# Revit family: LAMP_STORMBELL + OPAL REFLECTOR
name_source: partatom
category: Luminarias
revit_build: Autodesk Revit 2015 (Build: 20140606_1530(x64)
units: mm (PartAtom-declared; Revit-internal decimal feet)

## types (8) — shared parameters
CRI = 80
Diameter = 173 mm  [stored 0.567585 ft]
Fabricante = LAMP
Finish = Shiny white
Gear = Electronic
Height = 173 mm  [stored 0.567585 ft]
IEE = A+
Installation instructions = http://www.lamp.es
Insulation class = I
LED Lifetime = 50.000 L80 B10
Lamp = COB LED
Last update = 11/11/2020
Luminaire type = Indoor - Suspended Downlight
MacAdam = <3
Manufacturer URL = http://www.lamp.es
Manufacturer country = Spain
Manufacturer name = LAMP
Material COB = LAMP_COB
Material floron = LAMP_Aluminio cuerpo Stormbell
Photometric web file = Reflector glaseado : 2218LM 3000 WHITE FLOOD
Product URL = http://www.lamp.es
Product datasheet = http://www.lamp.es
Protection rating = IP20
Reflector product code = STBE420OP
Type = COB CITIZEN

## per-type parameters (varying)
| type | Descripción | Efficacy | Initial color | Initial intensity | Modelo | Plum | Power | Power Supply | Product code | Weight |
| 2218LM 3000 WHITE FLOOD | STORMBELL 3000 WW FL WH. | 84 lm/W | 3000 K | 2218 lm | ST117030FL830NBW | 26 W | 25 W | 220-240V 50-60Hz | ST117030FL830NBW | 4.50 kg |
| 2218LM 3000 WHITE WIDE FLOOD | STORMBELL 3000 WW WFL WH. | 84 lm/W | 3000 K | 2218 lm | ST117030WF830NBW | 26 W | 25 W | 220-240V 50-60Hz | ST117030WF830NBW | 4.50 kg |
| 2279LM 4000 WHITE FLOOD | STORMBELL 3000 NW FL WH. | 87 lm/W | 4000 K | 2279 lm | ST117030FL840NBW | 26 W | 25 W | 220-240V 50-60Hz | ST117030FL840NBW | 4.50 kg |
| 2279LM 4000 WHITE WIDE FLOOD | STORMBELL 3000 NW WFL WH. | 87 lm/W | 4000 K | 2279 lm | ST117030WF840NBW | 26 W | 25 W | 220-240V 50-60Hz | ST117030WF840NBW | 4.50 kg |
| 3351LM 3000 WHITE WIDE FLOOD | STORMBELL 5000 WW WFL WH. | 71 lm/W | 3000 K | 3351 lm | ST117050WF830NBW | 47 W | 44 W | 100-240V 50-60Hz | ST117050WF830NBW | 4.59 kg |
| 3394LM 3000 WHITE FLOOD | STORMBELL 5000 WW FL WH. | 72 lm/W | 3000 K | 3394 lm | ST117050FL830NBW | 47 W | 44 W | 100-240V 50-60Hz | ST117050FL830NBW | 4.59 kg |
| 3444LM 4000 WHITE WIDE FLOOD | STORMBELL 5000 NW WFL WH. | 73 lm/W | 4000 K | 3444 lm | ST117050WF840NBW | 47 W | 44 W | 100-240V 50-60Hz | ST117050WF840NBW | 4.59 kg |
| 3488LM 4000 WHITE FLOOD | STORMBELL 5000 NW FL WH. | 74 lm/W | 4000 K | 3488 lm | ST117050FL840NBW | 47 W | 44 W | 100-240V 50-60Hz | ST117050FL840NBW | 4.59 kg |

note: [stored X ft] marks values corroborated as IEEE doubles in the binary element streams (Revit-internal decimal feet)
